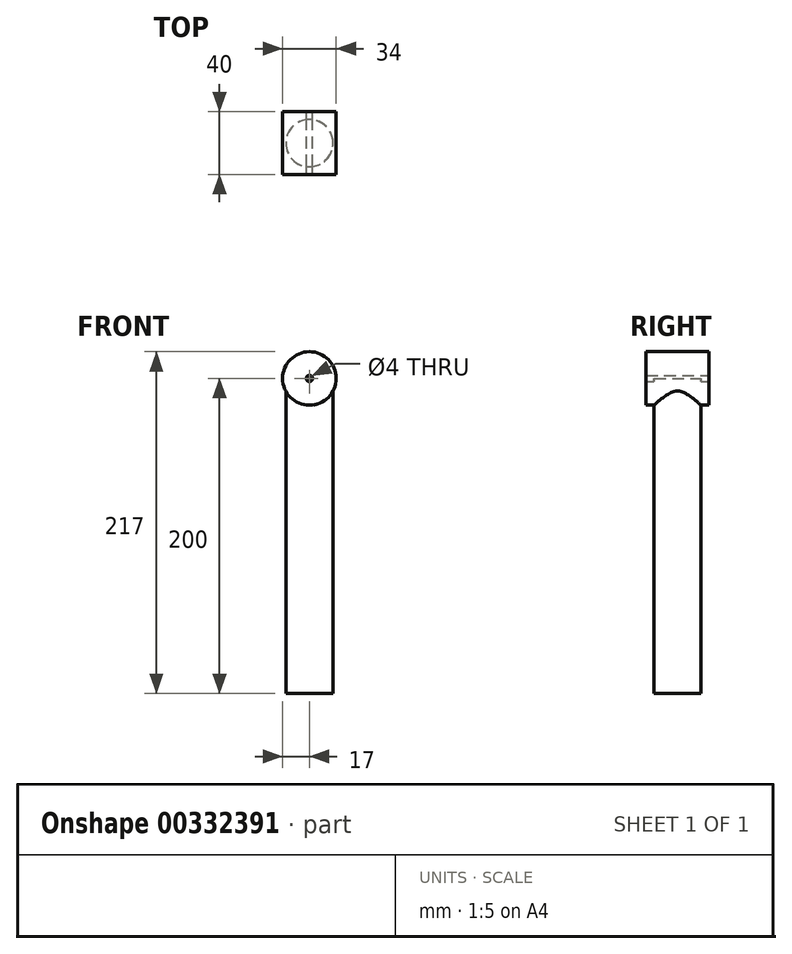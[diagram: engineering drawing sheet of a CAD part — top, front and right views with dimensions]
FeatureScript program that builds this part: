
annotation { "Feature Type Name" : "Feature", "Feature Type Description" : "" }
export const myFeature = defineFeature(function(context is Context, id is Id, definition is map)
    precondition{}
    {
        {
            var Q0;
            Q0=qCreatedBy(makeId("Front.planeOp"),FACE);
            var sketch = newSketch(context, id + "F0", { "sketchPlane" : qUnion([Q0])});
            skCircle(sketch, "E0", {"center": v(0, 0) * mm, "radius": 17 * mm});
            skCircle(sketch, "E1", {"center": v(0, 0) * mm, "radius": 2 * mm});
            skSolve(sketch);
        }
        {
            var Q0;
            Q0=makeQuery(id+"F0.imprint","IMPRINT",FACE,{"disambiguationData":[TD([[makeQuery(id+"F0.imprint","IMPRINT",EDGE,{"derivedFrom":sQuery(id+"F0.wireOp",EDGE,"E0")}),1.0]])]});
            extrude(context, id + "F1", {"entities" : qUnion([Q0]), "depth" : 40 * mm});
        }
        {
            var Q0;
            Q0=qCreatedBy(makeId("Top.planeOp"),FACE);
            var sketch = newSketch(context, id + "F2", { "sketchPlane" : qUnion([Q0])});
            skCircle(sketch, "E2", {"center": v(0, -20) * mm, "radius": 15 * mm});
            skSolve(sketch);
        }
        {
            var Q0;
            Q0 = qSketchRegion(id + "F2", true);
            extrude(context, id + "F3", {"entities" : qUnion([Q0]), "operationType" : NewBodyOperationType.ADD, "oppositeDirection" : true, "depth" : 200 * mm});
        }
    });
